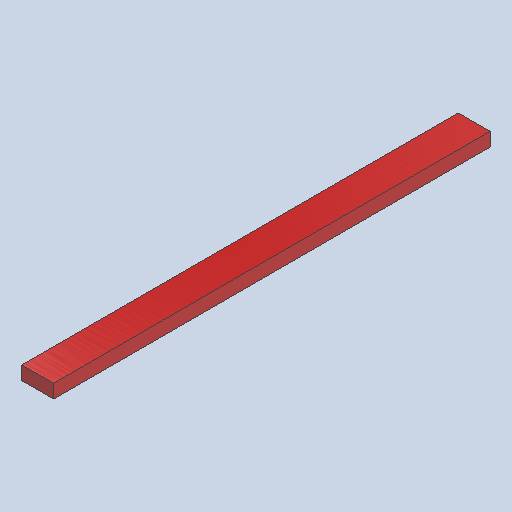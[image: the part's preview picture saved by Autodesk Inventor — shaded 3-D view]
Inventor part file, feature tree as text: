
AUTODESK INVENTOR PART (.ipt)
format: ipt  version: 2025 (Build 290162000, 162)  size: 95,744 bytes
history: native  units: in
note: dims shown in document units (in); Inventor stores cm internally (conversion verified against a paired STEP export)
features: other x4, sketch x1
ambient origin geometry x8: Origin, YZ Plane, XZ Plane, XY Plane, X Axis, Y Axis, Z Axis, Center Point
bodies: Solid1 (feature_tree)
feature tree (5):
  other  "4x2x4.ipt"
  other  "Solid1::4x2x4.ipt"
  other  "TaggingFeature1"
  sketch  "Sketch1"  dims[d0=0.3937in]
  other  "Finish1"
